# Revit family: Towel_Bar-American_Standard-Studio_S-7105_Series
name_source: partatom
category: Specialty Equipment
revit_build: Autodesk Revit 2018 (Build: 20170223_1515(x64)
units: mm (PartAtom-declared; Revit-internal decimal feet)

## family parameters
Cut with Voids When Loaded = No
Host = Face
OmniClass Number = 23.40.20.21.27
OmniClass Title = Towel Bars
Part Type = Normal
Room Calculation Point = No
Round Connector Dimension = Use Diameter
Shared = Yes

## types (6) — shared parameters
Assembly Code = C1030220
Default Elevation = 48"
Height = 2"
Installation Type = Wall Mounted
Manufacturer = American Standard
Price = Prices may vary. Please consult Manufacturer Representative for most up-to-date price list.
Product Documentation Link = https://www.americanstandard-us.com
Product Page URL = https://www.americanstandard-us.com
Revised Date = 05/03/2021
URL = https://www.americanstandard-us.com
Warranty Information = One Year General Product Warranty
Width = 3 7/8"

## per-type parameters (varying)
| type | Description | Finish | Length |
| 7105.018.002 | Studio S 18" Towel Bar | Metal-American_Standard-002-Polished_Chrome | 18" |
| 7105.024.002 | Studio S 24" Towel Bar | Metal-American_Standard-002-Polished_Chrome | 24" |
| 7105.024.295 | Studio S 24" Towel Bar | Metal-American_Standard-295-Brushed_Nickel | 24" |
| 7105.024.243 | Studio S 24" Towel Bar | Metal-American_Standard-243-Matte_Black | 24" |
| 7105.018.243 | Studio S 18" Towel Bar | Metal-American_Standard-243-Matte_Black | 18" |
| 7105.018.295 | Studio S 18" Towel Bar | Metal-American_Standard-295-Brushed_Nickel | 18" |

note: column(s) folded — value = type name in every type: Model

## geometry (parser evidence)
native form markers: Sweep x3
no freeform markers — native parametric forms only
